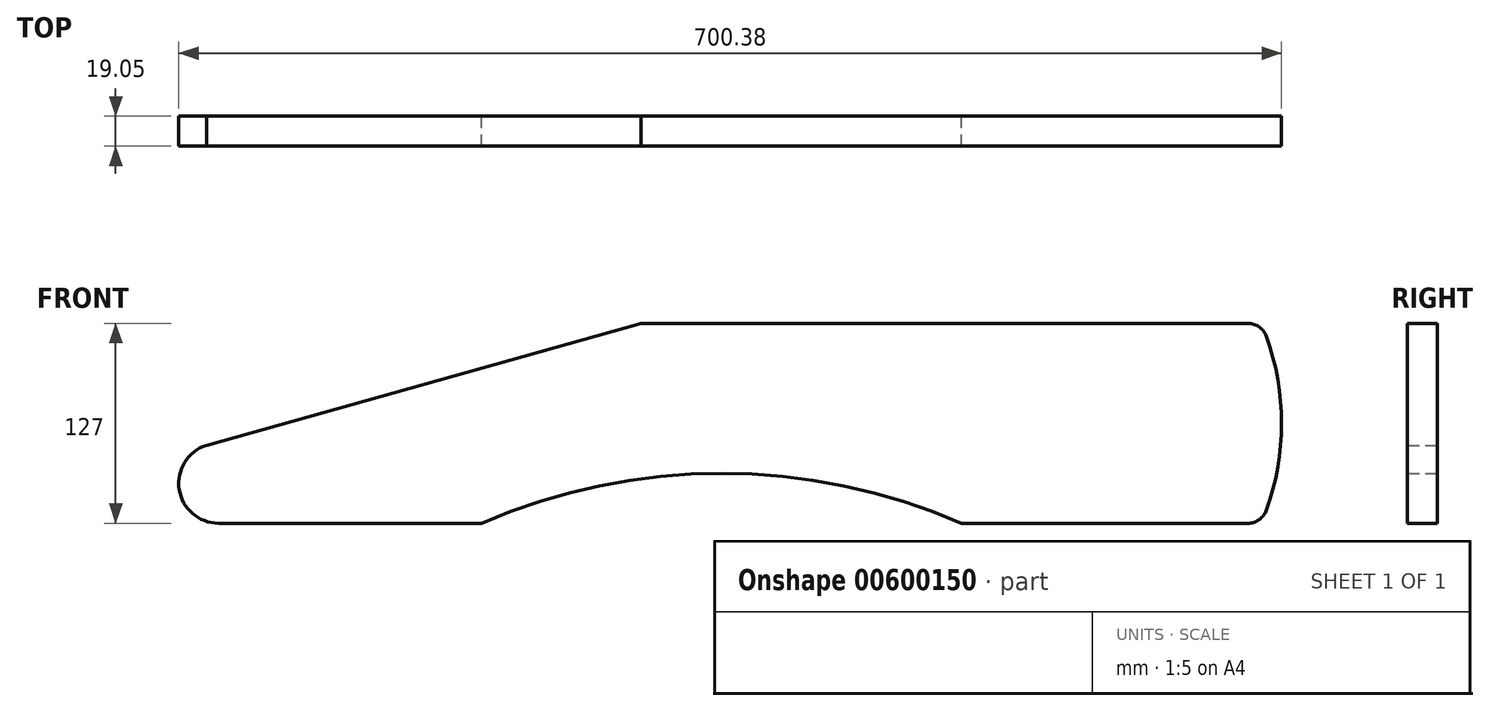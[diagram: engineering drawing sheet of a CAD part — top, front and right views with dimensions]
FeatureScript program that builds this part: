
annotation { "Feature Type Name" : "Feature", "Feature Type Description" : "" }
export const myFeature = defineFeature(function(context is Context, id is Id, definition is map)
    precondition{}
    {
        {
            var Q0;
            Q0=qCreatedBy(makeId("Front.planeOp"),FACE);
            var sketch = newSketch(context, id + "F0", { "sketchPlane" : qUnion([Q0])});
            skLineSegment(sketch, "E0.bottom", {"start": v(-56.86, 63.5) * mm, "end": v(328.63, 63.5) * mm});
            skLineSegment(sketch, "E0.top", {"start": v(-325.15, -63.5) * mm, "end": v(-157.96, -63.5) * mm});
            skLineSegment(sketch, "E1", {"start": v(350.04, 63.5) * mm, "end": v(-350.04, -63.5) * mm, "construction": true});
            skLineSegment(sketch, "E2", {"start": v(-332.74, -13.94) * mm, "end": v(-56.86, 63.5) * mm});
            skArc(sketch, "E3", {"start": v(-332.74, -13.94) * mm, "mid": v(-350.02, -41.94) * mm, "end": v(-325.15, -63.5) * mm});
            skArc(sketch, "E4", {"start": v(146.84, -63.5) * mm, "mid": v(-5.56, -31.82) * mm, "end": v(-157.96, -63.5) * mm});
            skArc(sketch, "E5", {"start": v(340.6, -55.04) * mm, "mid": v(350.07, 0) * mm, "end": v(340.6, 55.04) * mm});
            skPoint(sketch, "E6.visualSharp", {"position": v(337.34, 63.5) * mm});
            skArc(sketch, "E6.filletArc", {"start": v(340.6, 55.04) * mm, "mid": v(335.96, 61.17) * mm, "end": v(328.63, 63.5) * mm});
            skPoint(sketch, "E7.visualSharp", {"position": v(337.34, -63.5) * mm});
            skArc(sketch, "E7.filletArc", {"start": v(328.63, -63.5) * mm, "mid": v(335.96, -61.17) * mm, "end": v(340.6, -55.04) * mm});
            skLineSegment(sketch, "E8.trimOffspring", {"start": v(146.84, -63.5) * mm, "end": v(328.63, -63.5) * mm});
            skLineSegment(sketch, "E9", {"start": v(-350.02, -34.26) * mm, "end": v(-350.02, 96.13) * mm, "construction": true});
            skPoint(sketch, "E9.startSnap0", {"position": v(-350.02, -41.94) * mm});
            skLineSegment(sketch, "E10", {"start": v(350.07, 0) * mm, "end": v(350.07, 94.62) * mm, "construction": true});
            skSolve(sketch);
        }
        {
            var Q0;
            Q0 = qSketchRegion(id + "F0", true);
            extrude(context, id + "F1", {"entities" : qUnion([Q0]), "depth" : 19.05 * mm, "offsetDistance" : 25.4 * mm});
        }
    });
